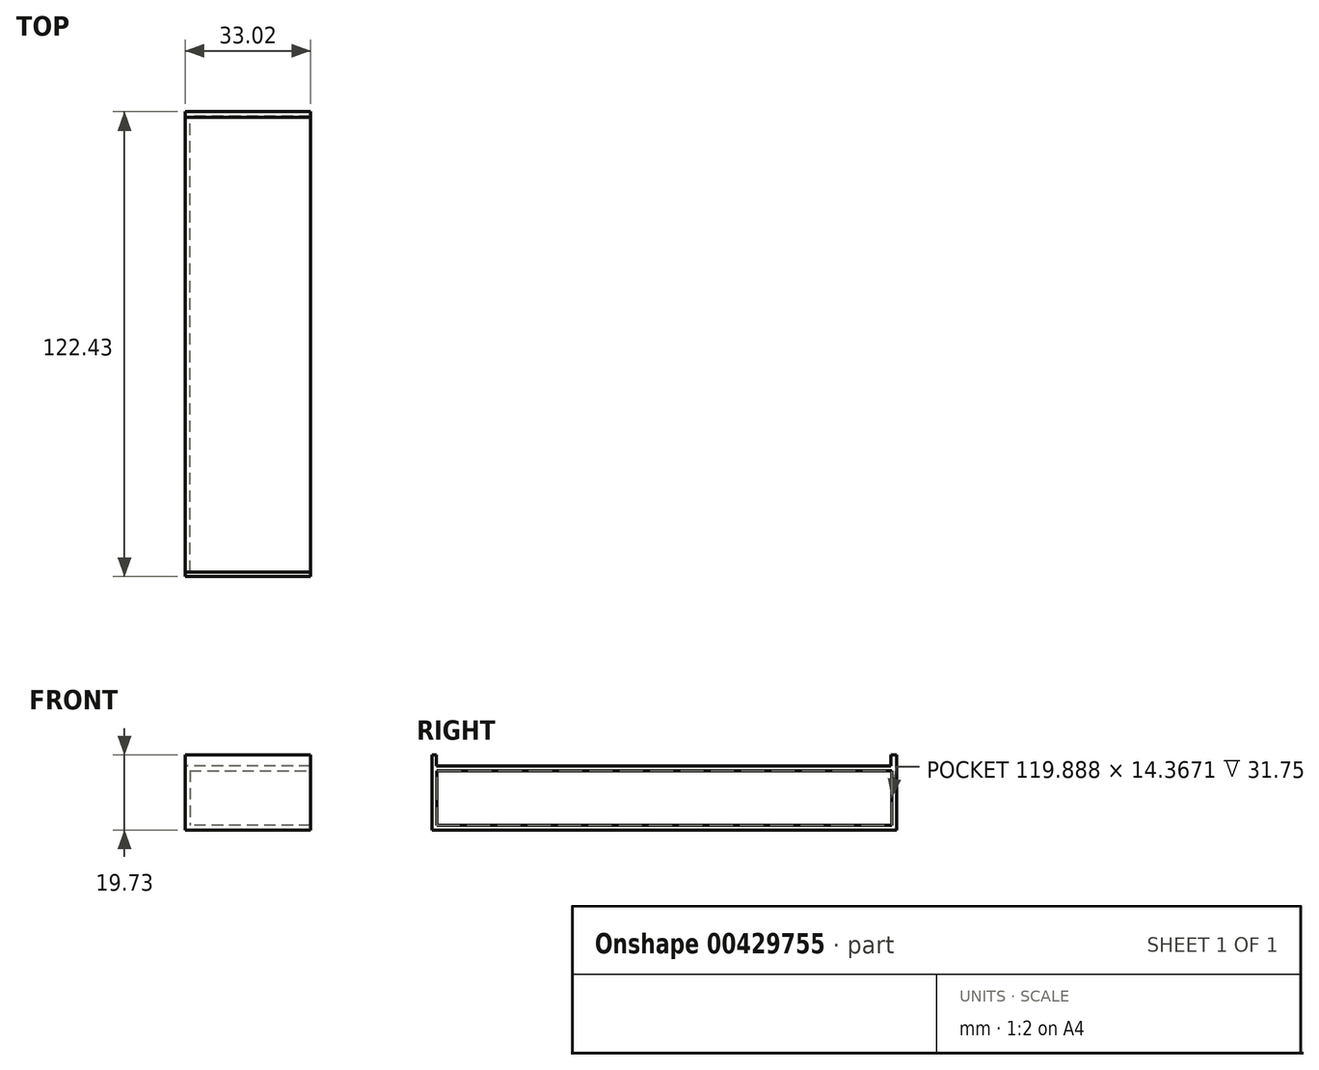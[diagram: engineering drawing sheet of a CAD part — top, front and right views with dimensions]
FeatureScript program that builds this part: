
annotation { "Feature Type Name" : "Feature", "Feature Type Description" : "" }
export const myFeature = defineFeature(function(context is Context, id is Id, definition is map)
    precondition{}
    {
        {
            var Q0;
            Q0=qCreatedBy(makeId("Right.planeOp"),FACE);
            var sketch = newSketch(context, id + "F0", { "sketchPlane" : qUnion([Q0])});
            skLineSegment(sketch, "E0.bottom", {"start": v(-76.27, 10.86) * mm, "end": v(46.16, 10.86) * mm});
            skLineSegment(sketch, "E0.top", {"start": v(-76.27, -8.87) * mm, "end": v(46.16, -8.87) * mm});
            skLineSegment(sketch, "E0.left", {"start": v(-76.27, 10.86) * mm, "end": v(-76.27, -8.87) * mm});
            skLineSegment(sketch, "E0.right", {"start": v(46.16, 10.86) * mm, "end": v(46.16, -8.87) * mm});
            skLineSegment(sketch, "E1.bottom", {"start": v(-75.08, 10.86) * mm, "end": v(44.68, 10.86) * mm});
            skLineSegment(sketch, "E1.top", {"start": v(-75.08, 8.04) * mm, "end": v(44.68, 8.04) * mm});
            skLineSegment(sketch, "E1.left", {"start": v(-75.08, 10.86) * mm, "end": v(-75.08, 8.04) * mm});
            skLineSegment(sketch, "E1.right", {"start": v(44.68, 10.86) * mm, "end": v(44.68, 8.04) * mm});
            skSolve(sketch);
        }
        {
            var Q0;
            Q0=makeQuery(id+"F0.imprint","IMPRINT",FACE,{"disambiguationData":[TD([[makeQuery(id+"F0.imprint","IMPRINT",EDGE,{"derivedFrom":sQuery(id+"F0.wireOp",EDGE,"E0.bottom")}),-1.0]])]});
            extrude(context, id + "F1", {"entities" : qUnion([Q0]), "depth" : 33.02 * mm});
        }
        {
            var Q0;
            Q0=makeQuery(id+"F1.opExtrude","CAP_FACE",FACE,{"disambiguationData":[OSD([sQuery(id+"F0.wireOp",EDGE,"E0.bottom"),sQuery(id+"F0.wireOp",EDGE,"E0.top"),sQuery(id+"F0.wireOp",EDGE,"E0.left"),sQuery(id+"F0.wireOp",EDGE,"E0.right")])],"isStart":false});
            shell(context, id + "F2", {"entities" : qUnion([Q0]), "thickness" : 1.27 * mm});
        }
    });
